# Revit family: equip-sink-elkay-s-lustrrtone-lr2522c
name_source: partatom
category: Plumbing Fixtures
units: mm (PartAtom-declared; Revit-internal decimal feet)

## family parameters
Always vertical = Yes
Cut with Voids When Loaded = No
OmniClass Number = 23.45.05.14.14.27
OmniClass Title = Service Sinks
Part Type = Normal
Room Calculation Point = No
Round Connector Dimension = Use Radius
Shared = No
Work Plane-Based = Yes

## types (4) — shared parameters
Assembly Code = D2010410
Back Faucet CL to Back = 0' - 1 3/4"
Back Faucet Hole One = Yes
Back Faucet Hole One Top = 0' - 0 3/4"
Back Faucet Hole One to CL = 0' - 4"
Back Faucet Hole Two = Yes
Back Faucet Hole Two Top = 0' - 0 3/4"
Bowl Drain Location FB = 0' - 7 7/8"
Bowl Length = 1' - 9"
Bowl Width = 1' - 3 3/4"
CW Flow Rate = 2 GPM
Default Elevation = 3' - 0"
Description = Lustertone Single Bowl Sink
Drain CL LR to Left Bowl Edge = 0' - 10 1/2"
Drain Material = Metal - Steel - Stainless - Chrome
Drain Part = LK18
Faucet Hole CL One to Two = 0' - 8"
Faucet Material = Metal - Steel - Stainless - Chrome
Faucet Part = LK810GN04T4
Faucet Plan = Yes
HW Flow Rate = 2 GPM
Manufacturer = Elkay Manufacturing
MasterFormat Number = 22.42.16.16
MasterFormat Title = Commercial Sinks
Minimum Cabinet Width = 24"
Nominal Dia = 0' - 0 3/8"
Nominal Radius = 0' - 0 3/16"
OmniClass Code = 23.45.05.14.14.27
OmniClass Title = Service Sinks
Sanitary Flow Rate = 10 GPM
Sanitary Nominal Dia = 0' - 1 1/2"
Sanitary Nominal Radius = 0' - 0 3/4"
Sink Ledge Back Width = 0' - 4 1/4"
Sink Ledge Back Width Hidden = 0' - 4 1/4"
Sink Ledge Front Width = 0' - 2"
Sink Ledge Front Width Hidden = 0' - 2"
Sink Ledge Left Width = 0' - 2"
Sink Ledge Left Width Hidden = 0' - 2"
Sink Ledge Right Width = 0' - 2"
Sink Ledge Right Width Hidden = 0' - 2"
Sink Length = 2' - 1"
Sink Material = Metal - Steel - Stainless - Chrome
Sink Width = 1' - 10"
Specification Sheet URL = http://www.elkayusa.com
Stem Material = Metal - Steel
URL = www.elkayusa.com
Wall Face to Back Face of Bowl = 0' - 6 1/4"
Wall Face to Drain Trap CL = 0' - 11 29/32"

## per-type parameters (varying)
| type | Bowl Depth | Model | Sink Part |
| LR2522C | 0' - 7 5/8" | LR2522C | LR25223 |
| LRAD252255C | 0' - 5 1/2" | LR252255C | LR2522553 |
| LRAD252265C | 0' - 6 1/2" | LRAD252265C | LRAD2522653 |
| LRAD252260C | 0' - 6" | LRAD252260C | LRAD2522603 |

## geometry (parser evidence)
native form markers: Sweep x12
no freeform markers — native parametric forms only
